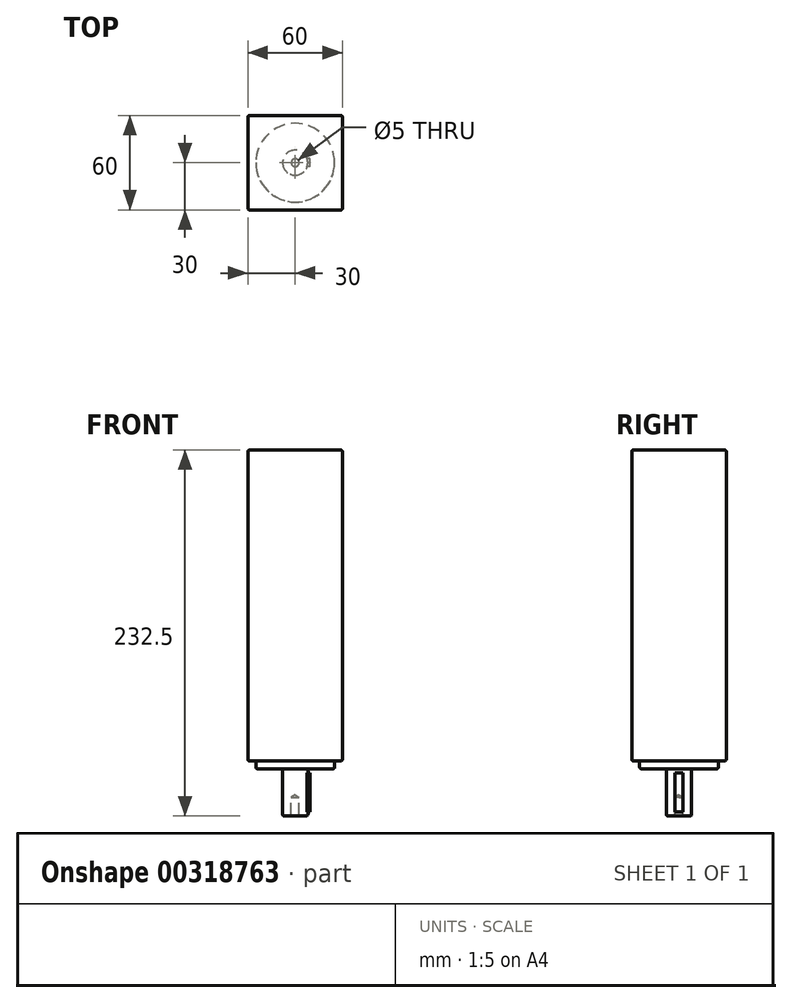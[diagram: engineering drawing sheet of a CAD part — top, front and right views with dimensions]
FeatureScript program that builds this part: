
annotation { "Feature Type Name" : "Feature", "Feature Type Description" : "" }
export const myFeature = defineFeature(function(context is Context, id is Id, definition is map)
    precondition{}
    {
        {
            var Q0;
            Q0=qCreatedBy(makeId("Top.planeOp"),FACE);
            var sketch = newSketch(context, id + "F0", { "sketchPlane" : qUnion([Q0])});
            skLineSegment(sketch, "E0.bottom", {"start": v(30, 30) * mm, "end": v(-30, 30) * mm});
            skLineSegment(sketch, "E0.top", {"start": v(30, -30) * mm, "end": v(-30, -30) * mm});
            skLineSegment(sketch, "E0.left", {"start": v(30, 30) * mm, "end": v(30, -30) * mm});
            skLineSegment(sketch, "E0.right", {"start": v(-30, 30) * mm, "end": v(-30, -30) * mm});
            skPoint(sketch, "E0.middle", {"position": v(0, 0) * mm});
            skSolve(sketch);
        }
        {
            var Q0;
            Q0=makeQuery(id+"F0.imprint","IMPRINT",FACE,{"disambiguationData":[TD([[makeQuery(id+"F0.imprint","IMPRINT",EDGE,{"derivedFrom":sQuery(id+"F0.wireOp",EDGE,"E0.bottom")}),1.0]])]});
            extrude(context, id + "F1", {"entities" : qUnion([Q0]), "depth" : 202.5 * mm, "offsetDistance" : 25 * mm});
        }
        {
            var Q0;
            Q0=makeQuery(id+"F1.opExtrude","CAP_FACE",FACE,{"disambiguationData":[OSD([sQuery(id+"F0.wireOp",EDGE,"E0.bottom"),sQuery(id+"F0.wireOp",EDGE,"E0.top"),sQuery(id+"F0.wireOp",EDGE,"E0.left"),sQuery(id+"F0.wireOp",EDGE,"E0.right")])],"isStart":true});
            var sketch = newSketch(context, id + "F2", { "sketchPlane" : qUnion([Q0])});
            skCircle(sketch, "E1", {"center": v(0, 0) * mm, "radius": 8 * mm});
            skSolve(sketch);
        }
        {
            var Q0;
            Q0=makeQuery(id+"F2.imprint","IMPRINT",FACE,{"disambiguationData":[TD([[makeQuery(id+"F2.imprint","IMPRINT",EDGE,{"derivedFrom":sQuery(id+"F2.wireOp",EDGE,"E1")}),1.0]])]});
            extrude(context, id + "F3", {"entities" : qUnion([Q0]), "operationType" : NewBodyOperationType.ADD, "depth" : 30 * mm, "offsetDistance" : 25 * mm});
        }
        {
            var Q0;
            Q0=makeQuery(id+"F3.opExtrude","CAP_FACE",FACE,{"disambiguationData":[OSD([sQuery(id+"F2.wireOp",EDGE,"E1")])],"isStart":false});
            var sketch = newSketch(context, id + "F4", { "sketchPlane" : qUnion([Q0])});
            skPoint(sketch, "E2", {"position": v(0, 0) * mm});
            skSolve(sketch);
        }
        {
            var Q0;
            Q0=sQuery(id+"F4.wireOp",VERTEX,"E2");
            var Q1;
            Q1=makeQuery(id+"F1.opExtrude","SWEPT_BODY",BODY,{"disambiguationData":[OSD([sQuery(id+"F0.wireOp",EDGE,"E0.bottom"),sQuery(id+"F0.wireOp",EDGE,"E0.top"),sQuery(id+"F0.wireOp",EDGE,"E0.left"),sQuery(id+"F0.wireOp",EDGE,"E0.right")])]});
            hole(context, id + "F5", {"style" : HoleStyle.SIMPLE, "endStyle" : HoleEndStyle.BLIND, "holeDiameter" : 5 * mm, "majorDiameter" : 5 * mm, "holeDepth" : 12 * mm, "tappedDepth" : 12 * mm, "tapClearance" : 3, "locations" : qUnion([Q0]), "scope" : qUnion([Q1])});
        }
        {
            var Q0;
            Q0=makeQuery(id+"F3.opExtrude","CAP_FACE",FACE,{"disambiguationData":[OSD([sQuery(id+"F2.wireOp",EDGE,"E1")])],"isStart":false});
            cPlane(context, id + "F6", {"entities" : qUnion([Q0]), "cplaneType" : CPlaneType.OFFSET, "offset" : 2.5 * mm, "oppositeDirection" : true, "width" : 150 * mm, "height" : 150 * mm});
        }
        {
            var Q0;
            Q0=qCreatedBy(id+"F6.planeOp",FACE);
            var sketch = newSketch(context, id + "F7", { "sketchPlane" : qUnion([Q0])});
            skLineSegment(sketch, "E3.bottom", {"start": v(9.42, 2.5) * mm, "end": v(6.42, 2.5) * mm});
            skLineSegment(sketch, "E3.top", {"start": v(9.42, -2.5) * mm, "end": v(6.42, -2.5) * mm});
            skLineSegment(sketch, "E3.left", {"start": v(9.42, 2.5) * mm, "end": v(9.42, -2.5) * mm});
            skLineSegment(sketch, "E3.right", {"start": v(6.42, 2.5) * mm, "end": v(6.42, -2.5) * mm});
            skPoint(sketch, "E3.middle", {"position": v(7.92, 0) * mm});
            skSolve(sketch);
        }
        {
            var Q0;
            Q0 = qSketchRegion(id + "F7", true);
            extrude(context, id + "F8", {"entities" : qUnion([Q0]), "operationType" : NewBodyOperationType.ADD, "oppositeDirection" : true, "depth" : 25 * mm, "offsetDistance" : 25 * mm});
        }
        {
            var Q0;
            Q0=makeQuery(id+"F1.opExtrude","CAP_FACE",FACE,{"disambiguationData":[OSD([sQuery(id+"F0.wireOp",EDGE,"E0.bottom"),sQuery(id+"F0.wireOp",EDGE,"E0.top"),sQuery(id+"F0.wireOp",EDGE,"E0.left"),sQuery(id+"F0.wireOp",EDGE,"E0.right")])],"isStart":true});
            var sketch = newSketch(context, id + "F9", { "sketchPlane" : qUnion([Q0])});
            skCircle(sketch, "E4", {"center": v(0, 0) * mm, "radius": 25 * mm});
            skLineSegment(sketch, "E5.bottom", {"start": v(33.33, 31.67) * mm, "end": v(-33.33, 31.67) * mm});
            skLineSegment(sketch, "E5.top", {"start": v(33.33, -31.67) * mm, "end": v(-33.33, -31.67) * mm});
            skLineSegment(sketch, "E5.left", {"start": v(33.33, 31.67) * mm, "end": v(33.33, -31.67) * mm});
            skLineSegment(sketch, "E5.right", {"start": v(-33.33, 31.67) * mm, "end": v(-33.33, -31.67) * mm});
            skSolve(sketch);
        }
        {
            var Q0;
            Q0=makeQuery(id+"F9.imprint","IMPRINT",FACE,{"disambiguationData":[TD([[makeQuery(id+"F9.imprint","IMPRINT",EDGE,{"derivedFrom":sQuery(id+"F9.wireOp",EDGE,"E4")}),-1.0]])]});
            var Q1;
            Q1=makeQuery(id+"F9.imprint","IMPRINT",FACE,{"disambiguationData":[TD([[makeQuery(id+"F9.imprint","IMPRINT",EDGE,{"derivedFrom":sQuery(id+"F9.wireOp",EDGE,"E5.bottom")}),1.0]])]});
            extrude(context, id + "F10", {"entities" : qUnion([Q0, Q1]), "operationType" : NewBodyOperationType.REMOVE, "oppositeDirection" : true, "depth" : 5 * mm, "offsetDistance" : 25 * mm});
        }
        {
            var Q0;
            Q0=makeQuery(id+"F10.boolean.opBoolean","COPY",FACE,{"derivedFrom":makeQuery(id+"F10.opExtrude","CAP_FACE",FACE,{"disambiguationData":[OSD([sQuery(id+"F9.wireOp",EDGE,"E4"),sQuery(id+"F9.wireOp",EDGE,"E5.bottom"),sQuery(id+"F9.wireOp",EDGE,"E5.top"),sQuery(id+"F9.wireOp",EDGE,"E5.left"),sQuery(id+"F9.wireOp",EDGE,"E5.right")])],"isStart":false})});
            var Q1;
            Q1=makeQuery(id+"F1.opExtrude","CAP_FACE",FACE,{"disambiguationData":[OSD([sQuery(id+"F0.wireOp",EDGE,"E0.bottom"),sQuery(id+"F0.wireOp",EDGE,"E0.top"),sQuery(id+"F0.wireOp",EDGE,"E0.left"),sQuery(id+"F0.wireOp",EDGE,"E0.right")])],"isStart":true});
            var Q2;
            Q2=makeQuery(id+"F3.opExtrude","CAP_FACE",FACE,{"disambiguationData":[OSD([sQuery(id+"F2.wireOp",EDGE,"E1")])],"isStart":false});
            var Q3;
            Q3=makeQuery(id+"F1.opExtrude","SWEPT_FACE",FACE,{"disambiguationData":[OSD([sQuery(id+"F0.wireOp",EDGE,"E0.right")])]});
            var Q4;
            Q4=makeQuery(id+"F1.opExtrude","SWEPT_FACE",FACE,{"disambiguationData":[OSD([sQuery(id+"F0.wireOp",EDGE,"E0.top")])]});
            var Q5;
            Q5=makeQuery(id+"F1.opExtrude","SWEPT_FACE",FACE,{"disambiguationData":[OSD([sQuery(id+"F0.wireOp",EDGE,"E0.bottom")])]});
            var Q6;
            Q6=makeQuery(id+"F1.opExtrude","SWEPT_FACE",FACE,{"disambiguationData":[OSD([sQuery(id+"F0.wireOp",EDGE,"E0.left")])]});
            fillet(context, id + "F11", {"entities" : qUnion([Q0, Q1, Q2, Q3, Q4, Q5, Q6]), "radius" : 1 * mm, "tangentPropagation" : true, "allowEdgeOverflow" : false});
        }
    });
